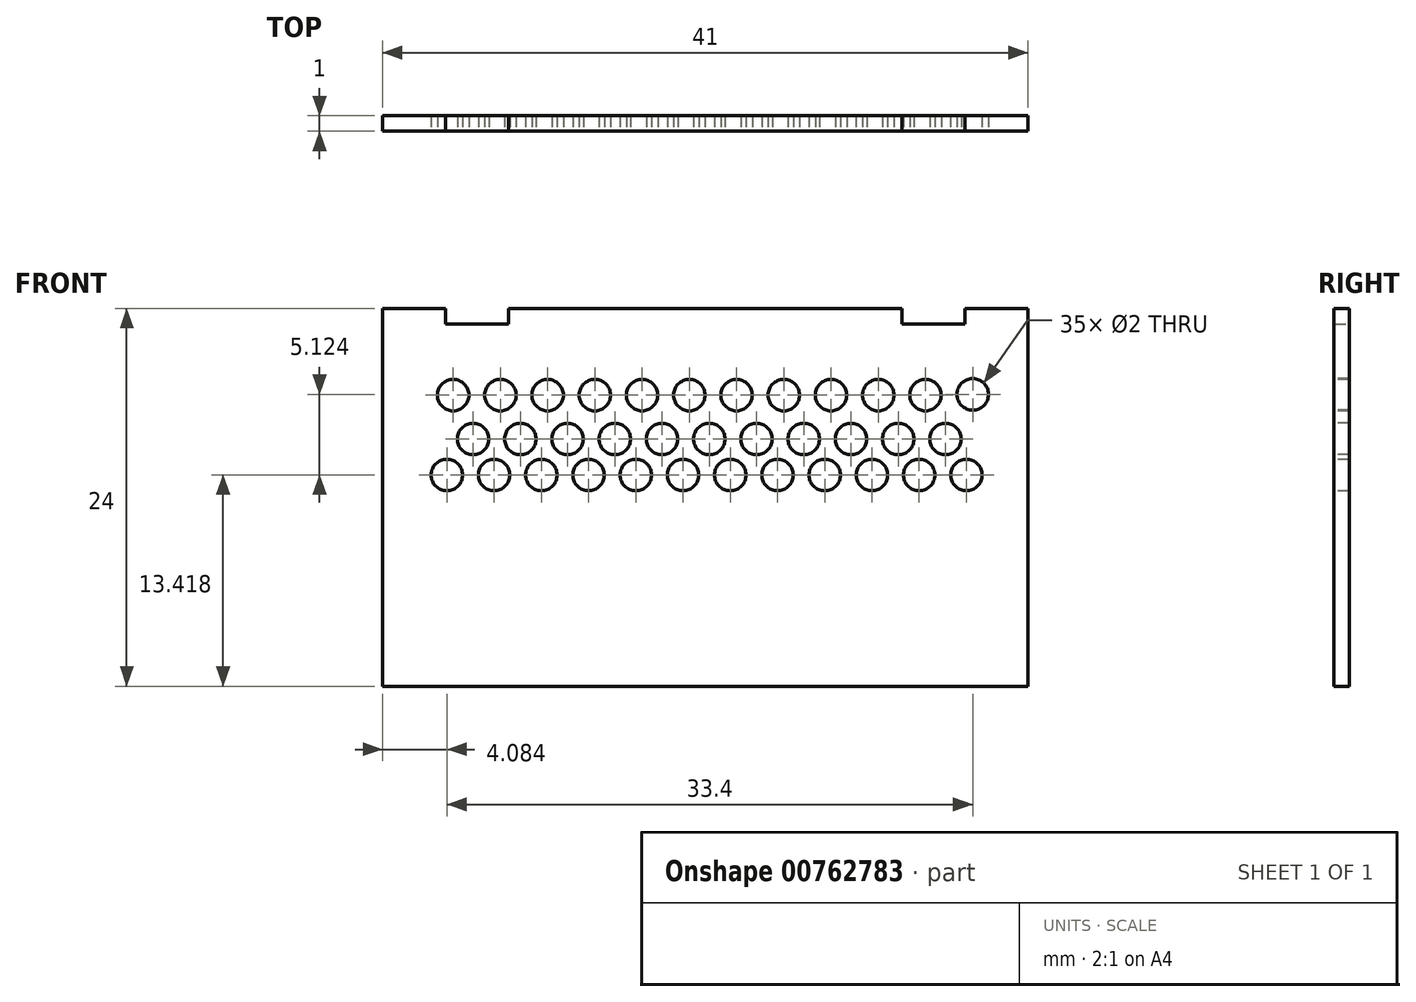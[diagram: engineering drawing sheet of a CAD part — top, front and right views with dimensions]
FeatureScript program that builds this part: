
annotation { "Feature Type Name" : "Feature", "Feature Type Description" : "" }
export const myFeature = defineFeature(function(context is Context, id is Id, definition is map)
    precondition{}
    {
        {
            var Q0;
            Q0=qCreatedBy(makeId("Front.planeOp"),FACE);
            var sketch = newSketch(context, id + "F0", { "sketchPlane" : qUnion([Q0])});
            skLineSegment(sketch, "E0", {"start": v(-22.92, 24) * mm, "end": v(-22.92, 0) * mm});
            skLineSegment(sketch, "E1", {"start": v(-22.92, 0) * mm, "end": v(18.08, 0) * mm});
            skLineSegment(sketch, "E2", {"start": v(18.08, 0) * mm, "end": v(18.08, 24) * mm});
            skLineSegment(sketch, "E3", {"start": v(18.08, 24) * mm, "end": v(14.08, 24) * mm});
            skLineSegment(sketch, "E4", {"start": v(-18.92, 24) * mm, "end": v(-18.92, 23) * mm});
            skLineSegment(sketch, "E5", {"start": v(-18.92, 23) * mm, "end": v(-14.92, 23) * mm});
            skLineSegment(sketch, "E6", {"start": v(-14.92, 23) * mm, "end": v(-14.92, 24) * mm});
            skLineSegment(sketch, "E7.trimOffspring", {"start": v(-18.92, 24) * mm, "end": v(-22.92, 24) * mm});
            skLineSegment(sketch, "E8", {"start": v(14.08, 24) * mm, "end": v(14.08, 23) * mm});
            skLineSegment(sketch, "E9", {"start": v(14.08, 23) * mm, "end": v(10.08, 23) * mm});
            skLineSegment(sketch, "E10", {"start": v(10.08, 23) * mm, "end": v(10.08, 24) * mm});
            skLineSegment(sketch, "E11.trimOffspring", {"start": v(10.08, 24) * mm, "end": v(-14.92, 24) * mm});
            skSolve(sketch);
        }
        {
            var Q0;
            Q0=makeQuery(id+"F0.imprint","IMPRINT",FACE,{"disambiguationData":[TD([[makeQuery(id+"F0.imprint","IMPRINT",EDGE,{"derivedFrom":sQuery(id+"F0.wireOp",EDGE,"E0")}),1.0]])]});
            extrude(context, id + "F1", {"entities" : qUnion([Q0]), "depth" : 1 * mm, "offsetDistance" : 25 * mm});
        }
        {
            var Q0;
            Q0=makeQuery(id+"F1.opExtrude","CAP_FACE",FACE,{"disambiguationData":[OSD([sQuery(id+"F0.wireOp",EDGE,"E0"),sQuery(id+"F0.wireOp",EDGE,"E1"),sQuery(id+"F0.wireOp",EDGE,"E2"),sQuery(id+"F0.wireOp",EDGE,"E3"),sQuery(id+"F0.wireOp",EDGE,"E4"),sQuery(id+"F0.wireOp",EDGE,"E5"),sQuery(id+"F0.wireOp",EDGE,"E6"),sQuery(id+"F0.wireOp",EDGE,"E7.trimOffspring"),sQuery(id+"F0.wireOp",EDGE,"E8"),sQuery(id+"F0.wireOp",EDGE,"E9"),sQuery(id+"F0.wireOp",EDGE,"E10"),sQuery(id+"F0.wireOp",EDGE,"E11.trimOffspring")])],"isStart":false});
            var sketch = newSketch(context, id + "F2", { "sketchPlane" : qUnion([Q0])});
            skCircle(sketch, "E12", {"center": v(-18.44, 18.5) * mm, "radius": 1 * mm});
            skCircle(sketch, "E13", {"center": v(-15.44, 18.5) * mm, "radius": 1 * mm});
            skCircle(sketch, "E14", {"center": v(-12.44, 18.5) * mm, "radius": 1 * mm});
            skCircle(sketch, "E15", {"center": v(-9.44, 18.5) * mm, "radius": 1 * mm});
            skCircle(sketch, "E16", {"center": v(-6.44, 18.5) * mm, "radius": 1 * mm});
            skCircle(sketch, "E17", {"center": v(-3.44, 18.5) * mm, "radius": 1 * mm});
            skCircle(sketch, "E18", {"center": v(-0.44, 18.5) * mm, "radius": 1 * mm});
            skCircle(sketch, "E19", {"center": v(2.56, 18.5) * mm, "radius": 1 * mm});
            skCircle(sketch, "E20", {"center": v(5.56, 18.5) * mm, "radius": 1 * mm});
            skCircle(sketch, "E21", {"center": v(8.56, 18.5) * mm, "radius": 1 * mm});
            skCircle(sketch, "E22", {"center": v(11.56, 18.5) * mm, "radius": 1 * mm});
            skCircle(sketch, "E23", {"center": v(14.56, 18.54) * mm, "radius": 1 * mm});
            skSolve(sketch);
        }
        {
            var Q0;
            Q0 = qSketchRegion(id + "F2", true);
            extrude(context, id + "F3", {"entities" : qUnion([Q0]), "operationType" : NewBodyOperationType.REMOVE, "endBound" : BoundingType.THROUGH_ALL, "oppositeDirection" : true, "depth" : 25 * mm, "offsetDistance" : 25 * mm});
        }
        {
            var Q0;
            Q0=makeQuery(id+"F1.opExtrude","CAP_FACE",FACE,{"disambiguationData":[OSD([sQuery(id+"F0.wireOp",EDGE,"E0"),sQuery(id+"F0.wireOp",EDGE,"E1"),sQuery(id+"F0.wireOp",EDGE,"E2"),sQuery(id+"F0.wireOp",EDGE,"E3"),sQuery(id+"F0.wireOp",EDGE,"E4"),sQuery(id+"F0.wireOp",EDGE,"E5"),sQuery(id+"F0.wireOp",EDGE,"E6"),sQuery(id+"F0.wireOp",EDGE,"E7.trimOffspring"),sQuery(id+"F0.wireOp",EDGE,"E8"),sQuery(id+"F0.wireOp",EDGE,"E9"),sQuery(id+"F0.wireOp",EDGE,"E10"),sQuery(id+"F0.wireOp",EDGE,"E11.trimOffspring")])],"isStart":false});
            var sketch = newSketch(context, id + "F4", { "sketchPlane" : qUnion([Q0])});
            skCircle(sketch, "E24", {"center": v(-17.17, 15.7) * mm, "radius": 1 * mm});
            skCircle(sketch, "E25", {"center": v(-14.17, 15.7) * mm, "radius": 1 * mm});
            skCircle(sketch, "E26", {"center": v(-11.17, 15.7) * mm, "radius": 1 * mm});
            skCircle(sketch, "E27", {"center": v(-8.17, 15.7) * mm, "radius": 1 * mm});
            skCircle(sketch, "E28", {"center": v(-5.17, 15.7) * mm, "radius": 1 * mm});
            skCircle(sketch, "E29", {"center": v(-2.17, 15.7) * mm, "radius": 1 * mm});
            skCircle(sketch, "E30", {"center": v(0.83, 15.7) * mm, "radius": 1 * mm});
            skCircle(sketch, "E31", {"center": v(3.83, 15.7) * mm, "radius": 1 * mm});
            skCircle(sketch, "E32", {"center": v(6.83, 15.7) * mm, "radius": 1 * mm});
            skCircle(sketch, "E33", {"center": v(9.83, 15.7) * mm, "radius": 1 * mm});
            skCircle(sketch, "E34", {"center": v(12.83, 15.7) * mm, "radius": 1 * mm});
            skSolve(sketch);
        }
        {
            var Q0;
            Q0=makeQuery(id+"F4.imprint","IMPRINT",FACE,{"disambiguationData":[TD([[makeQuery(id+"F4.imprint","IMPRINT",EDGE,{"derivedFrom":sQuery(id+"F4.wireOp",EDGE,"E24")}),1.0]])]});
            var Q1;
            Q1=makeQuery(id+"F4.imprint","IMPRINT",FACE,{"disambiguationData":[TD([[makeQuery(id+"F4.imprint","IMPRINT",EDGE,{"derivedFrom":sQuery(id+"F4.wireOp",EDGE,"E25")}),1.0]])]});
            var Q2;
            Q2=makeQuery(id+"F4.imprint","IMPRINT",FACE,{"disambiguationData":[TD([[makeQuery(id+"F4.imprint","IMPRINT",EDGE,{"derivedFrom":sQuery(id+"F4.wireOp",EDGE,"E26")}),1.0]])]});
            var Q3;
            Q3=makeQuery(id+"F4.imprint","IMPRINT",FACE,{"disambiguationData":[TD([[makeQuery(id+"F4.imprint","IMPRINT",EDGE,{"derivedFrom":sQuery(id+"F4.wireOp",EDGE,"E27")}),1.0]])]});
            var Q4;
            Q4=makeQuery(id+"F4.imprint","IMPRINT",FACE,{"disambiguationData":[TD([[makeQuery(id+"F4.imprint","IMPRINT",EDGE,{"derivedFrom":sQuery(id+"F4.wireOp",EDGE,"E28")}),1.0]])]});
            var Q5;
            Q5=makeQuery(id+"F4.imprint","IMPRINT",FACE,{"disambiguationData":[TD([[makeQuery(id+"F4.imprint","IMPRINT",EDGE,{"derivedFrom":sQuery(id+"F4.wireOp",EDGE,"E29")}),1.0]])]});
            var Q6;
            Q6=makeQuery(id+"F4.imprint","IMPRINT",FACE,{"disambiguationData":[TD([[makeQuery(id+"F4.imprint","IMPRINT",EDGE,{"derivedFrom":sQuery(id+"F4.wireOp",EDGE,"E30")}),1.0]])]});
            var Q7;
            Q7=makeQuery(id+"F4.imprint","IMPRINT",FACE,{"disambiguationData":[TD([[makeQuery(id+"F4.imprint","IMPRINT",EDGE,{"derivedFrom":sQuery(id+"F4.wireOp",EDGE,"E31")}),1.0]])]});
            var Q8;
            Q8=makeQuery(id+"F4.imprint","IMPRINT",FACE,{"disambiguationData":[TD([[makeQuery(id+"F4.imprint","IMPRINT",EDGE,{"derivedFrom":sQuery(id+"F4.wireOp",EDGE,"E32")}),1.0]])]});
            var Q9;
            Q9=makeQuery(id+"F4.imprint","IMPRINT",FACE,{"disambiguationData":[TD([[makeQuery(id+"F4.imprint","IMPRINT",EDGE,{"derivedFrom":sQuery(id+"F4.wireOp",EDGE,"E33")}),1.0]])]});
            var Q10;
            Q10=makeQuery(id+"F4.imprint","IMPRINT",FACE,{"disambiguationData":[TD([[makeQuery(id+"F4.imprint","IMPRINT",EDGE,{"derivedFrom":sQuery(id+"F4.wireOp",EDGE,"E34")}),1.0]])]});
            extrude(context, id + "F5", {"entities" : qUnion([Q0, Q1, Q2, Q3, Q4, Q5, Q6, Q7, Q8, Q9, Q10]), "operationType" : NewBodyOperationType.REMOVE, "endBound" : BoundingType.THROUGH_ALL, "oppositeDirection" : true, "depth" : 25 * mm, "offsetDistance" : 25 * mm});
        }
        {
            var Q0;
            Q0=makeQuery(id+"F1.opExtrude","CAP_FACE",FACE,{"disambiguationData":[OSD([sQuery(id+"F0.wireOp",EDGE,"E0"),sQuery(id+"F0.wireOp",EDGE,"E1"),sQuery(id+"F0.wireOp",EDGE,"E2"),sQuery(id+"F0.wireOp",EDGE,"E3"),sQuery(id+"F0.wireOp",EDGE,"E4"),sQuery(id+"F0.wireOp",EDGE,"E5"),sQuery(id+"F0.wireOp",EDGE,"E6"),sQuery(id+"F0.wireOp",EDGE,"E7.trimOffspring"),sQuery(id+"F0.wireOp",EDGE,"E8"),sQuery(id+"F0.wireOp",EDGE,"E9"),sQuery(id+"F0.wireOp",EDGE,"E10"),sQuery(id+"F0.wireOp",EDGE,"E11.trimOffspring")])],"isStart":false});
            var sketch = newSketch(context, id + "F6", { "sketchPlane" : qUnion([Q0])});
            skCircle(sketch, "E35", {"center": v(14.16, 13.42) * mm, "radius": 1 * mm});
            skCircle(sketch, "E36", {"center": v(11.16, 13.42) * mm, "radius": 1 * mm});
            skCircle(sketch, "E37", {"center": v(8.16, 13.42) * mm, "radius": 1 * mm});
            skCircle(sketch, "E38", {"center": v(5.16, 13.42) * mm, "radius": 1 * mm});
            skCircle(sketch, "E39", {"center": v(2.16, 13.42) * mm, "radius": 1 * mm});
            skCircle(sketch, "E40", {"center": v(-0.84, 13.42) * mm, "radius": 1 * mm});
            skCircle(sketch, "E41", {"center": v(-3.84, 13.42) * mm, "radius": 1 * mm});
            skCircle(sketch, "E42", {"center": v(-6.84, 13.42) * mm, "radius": 1 * mm});
            skCircle(sketch, "E43", {"center": v(-9.84, 13.42) * mm, "radius": 1 * mm});
            skCircle(sketch, "E44", {"center": v(-12.84, 13.42) * mm, "radius": 1 * mm});
            skCircle(sketch, "E45", {"center": v(-15.84, 13.42) * mm, "radius": 1 * mm});
            skCircle(sketch, "E46", {"center": v(-18.84, 13.42) * mm, "radius": 1 * mm});
            skSolve(sketch);
        }
        {
            var Q0;
            Q0=makeQuery(id+"F6.imprint","IMPRINT",FACE,{"disambiguationData":[TD([[makeQuery(id+"F6.imprint","IMPRINT",EDGE,{"derivedFrom":sQuery(id+"F6.wireOp",EDGE,"E44")}),1.0]])]});
            var Q1;
            Q1=makeQuery(id+"F6.imprint","IMPRINT",FACE,{"disambiguationData":[TD([[makeQuery(id+"F6.imprint","IMPRINT",EDGE,{"derivedFrom":sQuery(id+"F6.wireOp",EDGE,"E46")}),1.0]])]});
            var Q2;
            Q2=makeQuery(id+"F6.imprint","IMPRINT",FACE,{"disambiguationData":[TD([[makeQuery(id+"F6.imprint","IMPRINT",EDGE,{"derivedFrom":sQuery(id+"F6.wireOp",EDGE,"E45")}),1.0]])]});
            var Q3;
            Q3=makeQuery(id+"F6.imprint","IMPRINT",FACE,{"disambiguationData":[TD([[makeQuery(id+"F6.imprint","IMPRINT",EDGE,{"derivedFrom":sQuery(id+"F6.wireOp",EDGE,"E43")}),1.0]])]});
            var Q4;
            Q4=makeQuery(id+"F6.imprint","IMPRINT",FACE,{"disambiguationData":[TD([[makeQuery(id+"F6.imprint","IMPRINT",EDGE,{"derivedFrom":sQuery(id+"F6.wireOp",EDGE,"E42")}),1.0]])]});
            var Q5;
            Q5=makeQuery(id+"F6.imprint","IMPRINT",FACE,{"disambiguationData":[TD([[makeQuery(id+"F6.imprint","IMPRINT",EDGE,{"derivedFrom":sQuery(id+"F6.wireOp",EDGE,"E41")}),1.0]])]});
            var Q6;
            Q6=makeQuery(id+"F6.imprint","IMPRINT",FACE,{"disambiguationData":[TD([[makeQuery(id+"F6.imprint","IMPRINT",EDGE,{"derivedFrom":sQuery(id+"F6.wireOp",EDGE,"E40")}),1.0]])]});
            var Q7;
            Q7=makeQuery(id+"F6.imprint","IMPRINT",FACE,{"disambiguationData":[TD([[makeQuery(id+"F6.imprint","IMPRINT",EDGE,{"derivedFrom":sQuery(id+"F6.wireOp",EDGE,"E39")}),1.0]])]});
            var Q8;
            Q8=makeQuery(id+"F6.imprint","IMPRINT",FACE,{"disambiguationData":[TD([[makeQuery(id+"F6.imprint","IMPRINT",EDGE,{"derivedFrom":sQuery(id+"F6.wireOp",EDGE,"E38")}),1.0]])]});
            var Q9;
            Q9=makeQuery(id+"F6.imprint","IMPRINT",FACE,{"disambiguationData":[TD([[makeQuery(id+"F6.imprint","IMPRINT",EDGE,{"derivedFrom":sQuery(id+"F6.wireOp",EDGE,"E37")}),1.0]])]});
            var Q10;
            Q10=makeQuery(id+"F6.imprint","IMPRINT",FACE,{"disambiguationData":[TD([[makeQuery(id+"F6.imprint","IMPRINT",EDGE,{"derivedFrom":sQuery(id+"F6.wireOp",EDGE,"E36")}),1.0]])]});
            var Q11;
            Q11=makeQuery(id+"F6.imprint","IMPRINT",FACE,{"disambiguationData":[TD([[makeQuery(id+"F6.imprint","IMPRINT",EDGE,{"derivedFrom":sQuery(id+"F6.wireOp",EDGE,"E35")}),1.0]])]});
            var Q12;
            Q12=sQuery(id+"F6.wireOp",EDGE,"E46");
            var Q13;
            Q13=sQuery(id+"F6.wireOp",EDGE,"E45");
            var Q14;
            Q14=sQuery(id+"F6.wireOp",EDGE,"E44");
            var Q15;
            Q15=sQuery(id+"F6.wireOp",EDGE,"E43");
            var Q16;
            Q16=sQuery(id+"F6.wireOp",EDGE,"E42");
            var Q17;
            Q17=sQuery(id+"F6.wireOp",EDGE,"E41");
            var Q18;
            Q18=sQuery(id+"F6.wireOp",EDGE,"E40");
            var Q19;
            Q19=sQuery(id+"F6.wireOp",EDGE,"E39");
            var Q20;
            Q20=sQuery(id+"F6.wireOp",EDGE,"E38");
            var Q21;
            Q21=sQuery(id+"F6.wireOp",EDGE,"E37");
            var Q22;
            Q22=sQuery(id+"F6.wireOp",EDGE,"E36");
            var Q23;
            Q23=sQuery(id+"F6.wireOp",EDGE,"E35");
            extrude(context, id + "F7", {"entities" : qUnion([Q0, Q1, Q2, Q3, Q4, Q5, Q6, Q7, Q8, Q9, Q10, Q11]), "operationType" : NewBodyOperationType.REMOVE, "surfaceEntities" : qUnion([Q12, Q13, Q14, Q15, Q16, Q17, Q18, Q19, Q20, Q21, Q22, Q23]), "endBound" : BoundingType.THROUGH_ALL, "oppositeDirection" : true, "depth" : 25 * mm, "offsetDistance" : 25 * mm});
        }
    });
